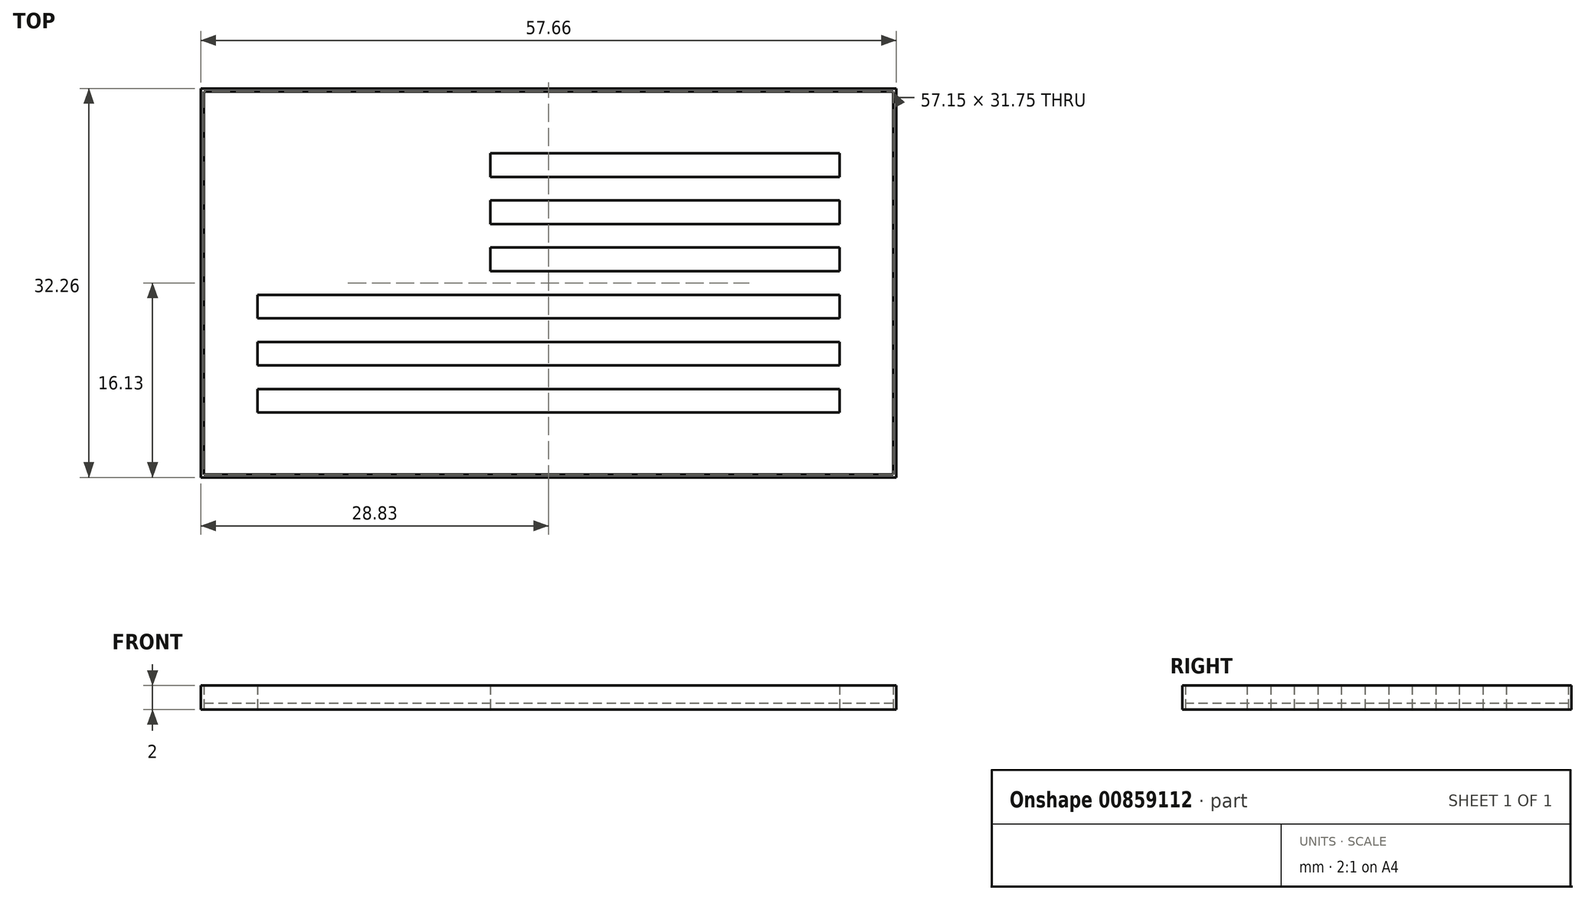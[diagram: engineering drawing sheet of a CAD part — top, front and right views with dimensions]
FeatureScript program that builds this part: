
annotation { "Feature Type Name" : "Feature", "Feature Type Description" : "" }
export const myFeature = defineFeature(function(context is Context, id is Id, definition is map)
    precondition{}
    {
        {
            var Q0;
            Q0=qCreatedBy(makeId("Top.planeOp"),FACE);
            var sketch = newSketch(context, id + "F0", { "sketchPlane" : qUnion([Q0])});
            skLineSegment(sketch, "E0.rect.bottom", {"start": v(24.13, 12.7) * mm, "end": v(-24.13, 12.7) * mm});
            skLineSegment(sketch, "E0.rect.top", {"start": v(24.13, -12.7) * mm, "end": v(-24.13, -12.7) * mm});
            skLineSegment(sketch, "E0.rect.left", {"start": v(24.13, 12.7) * mm, "end": v(24.13, -12.7) * mm});
            skLineSegment(sketch, "E0.rect.right", {"start": v(-24.13, 12.7) * mm, "end": v(-24.13, -12.7) * mm});
            skPoint(sketch, "E0.rect.middle", {"position": v(0, 0) * mm});
            skLineSegment(sketch, "E1.bottom", {"start": v(-24.13, 12.7) * mm, "end": v(-4.83, 12.7) * mm});
            skLineSegment(sketch, "E1.top", {"start": v(-24.13, -0.98) * mm, "end": v(-4.83, -0.98) * mm});
            skLineSegment(sketch, "E1.left", {"start": v(-24.13, 12.7) * mm, "end": v(-24.13, -0.98) * mm});
            skLineSegment(sketch, "E1.right", {"start": v(-4.83, 12.7) * mm, "end": v(-4.83, -0.98) * mm});
            skLineSegment(sketch, "E2.bottom", {"start": v(-4.83, 12.7) * mm, "end": v(24.13, 12.7) * mm});
            skLineSegment(sketch, "E2.top", {"start": v(-4.83, 10.75) * mm, "end": v(24.13, 10.75) * mm});
            skLineSegment(sketch, "E2.left", {"start": v(-4.83, 12.7) * mm, "end": v(-4.83, 10.75) * mm});
            skLineSegment(sketch, "E2.right", {"start": v(24.13, 12.7) * mm, "end": v(24.13, 10.75) * mm});
            skLineSegment(sketch, "E3.MirrorCS", {"start": v(-4.83, 8.8) * mm, "end": v(24.13, 8.8) * mm});
            skLineSegment(sketch, "E4.MirrorCS", {"start": v(-4.83, 6.84) * mm, "end": v(24.13, 6.84) * mm});
            skLineSegment(sketch, "E5.MirrorCS", {"start": v(-4.83, 4.89) * mm, "end": v(24.13, 4.89) * mm});
            skLineSegment(sketch, "E6.MirrorCS", {"start": v(-4.83, 2.93) * mm, "end": v(24.13, 2.93) * mm});
            skLineSegment(sketch, "E7.MirrorCS", {"start": v(-4.83, 0.98) * mm, "end": v(24.13, 0.98) * mm});
            skLineSegment(sketch, "E8.MirrorCS", {"start": v(-4.83, -0.97) * mm, "end": v(24.13, -0.97) * mm});
            skLineSegment(sketch, "E9.bottom", {"start": v(-24.13, -0.98) * mm, "end": v(24.13, -0.98) * mm});
            skLineSegment(sketch, "E9.top", {"start": v(-24.13, -2.93) * mm, "end": v(24.13, -2.93) * mm});
            skLineSegment(sketch, "E9.left", {"start": v(-24.13, -0.98) * mm, "end": v(-24.13, -2.93) * mm});
            skLineSegment(sketch, "E9.right", {"start": v(24.13, -0.98) * mm, "end": v(24.13, -2.93) * mm});
            skLineSegment(sketch, "E10.MirrorCS", {"start": v(-24.13, -4.88) * mm, "end": v(24.13, -4.88) * mm});
            skLineSegment(sketch, "E11.MirrorCS", {"start": v(-24.13, -6.84) * mm, "end": v(24.13, -6.84) * mm});
            skLineSegment(sketch, "E12.MirrorCS", {"start": v(-24.13, -8.8) * mm, "end": v(24.13, -8.8) * mm});
            skLineSegment(sketch, "E13.MirrorCS", {"start": v(-24.13, -10.74) * mm, "end": v(24.13, -10.74) * mm});
            skLineSegment(sketch, "E14.bottom", {"start": v(-24.13, 12.7) * mm, "end": v(-22.53, 12.7) * mm});
            skLineSegment(sketch, "E14.left", {"start": v(-24.13, 12.7) * mm, "end": v(-24.13, 11.33) * mm});
            skPoint(sketch, "E15.cCircle.perimeterSnap0", {"position": v(-22.53, 12.01) * mm});
            skPoint(sketch, "E15.0.startSnap0", {"position": v(-22.53, 12.01) * mm});
            skLineSegment(sketch, "E16", {"start": v(-22.53, 12.12) * mm, "end": v(-22.35, 11.57) * mm});
            skLineSegment(sketch, "E17", {"start": v(-21.78, 11.57) * mm, "end": v(-22.35, 11.57) * mm});
            skLineSegment(sketch, "E18", {"start": v(-23, 10.7) * mm, "end": v(-22.82, 11.24) * mm});
            skLineSegment(sketch, "E19", {"start": v(-23.28, 11.57) * mm, "end": v(-22.82, 11.24) * mm});
            skLineSegment(sketch, "E20", {"start": v(-21.78, 11.57) * mm, "end": v(-22.24, 11.24) * mm});
            skLineSegment(sketch, "E21.trimOffspring", {"start": v(-22.24, 11.24) * mm, "end": v(-22.07, 10.7) * mm});
            skLineSegment(sketch, "E22.trimOffspring", {"start": v(-22.53, 11.03) * mm, "end": v(-23, 10.7) * mm});
            skLineSegment(sketch, "E23.trimOffspring", {"start": v(-22.53, 11.03) * mm, "end": v(-22.07, 10.7) * mm});
            skLineSegment(sketch, "E24.trimOffspring", {"start": v(-22.7, 11.57) * mm, "end": v(-22.53, 12.12) * mm});
            skLineSegment(sketch, "E25.trimOffspring", {"start": v(-22.7, 11.57) * mm, "end": v(-23.28, 11.57) * mm});
            skLineSegment(sketch, "E26.0.1.0", {"start": v(-22.53, 9.37) * mm, "end": v(-22.35, 8.83) * mm});
            skLineSegment(sketch, "E26.0.1.1", {"start": v(-21.78, 8.83) * mm, "end": v(-22.35, 8.83) * mm});
            skLineSegment(sketch, "E26.0.1.2", {"start": v(-21.78, 8.83) * mm, "end": v(-22.24, 8.5) * mm});
            skLineSegment(sketch, "E26.0.1.3", {"start": v(-22.24, 8.5) * mm, "end": v(-22.07, 7.95) * mm});
            skLineSegment(sketch, "E26.0.1.4", {"start": v(-22.53, 8.28) * mm, "end": v(-22.07, 7.95) * mm});
            skLineSegment(sketch, "E26.0.1.5", {"start": v(-22.53, 8.28) * mm, "end": v(-23, 7.95) * mm});
            skLineSegment(sketch, "E26.0.1.6", {"start": v(-23, 7.95) * mm, "end": v(-22.82, 8.5) * mm});
            skLineSegment(sketch, "E26.0.1.7", {"start": v(-23.28, 8.83) * mm, "end": v(-22.82, 8.5) * mm});
            skLineSegment(sketch, "E26.0.1.8", {"start": v(-22.7, 8.83) * mm, "end": v(-22.53, 9.37) * mm});
            skLineSegment(sketch, "E26.0.1.9", {"start": v(-22.7, 8.83) * mm, "end": v(-23.28, 8.83) * mm});
            skLineSegment(sketch, "E26.0.2.0", {"start": v(-22.53, 6.63) * mm, "end": v(-22.35, 6.09) * mm});
            skLineSegment(sketch, "E26.0.2.1", {"start": v(-21.78, 6.09) * mm, "end": v(-22.35, 6.09) * mm});
            skLineSegment(sketch, "E26.0.2.2", {"start": v(-21.78, 6.09) * mm, "end": v(-22.24, 5.75) * mm});
            skLineSegment(sketch, "E26.0.2.3", {"start": v(-22.24, 5.75) * mm, "end": v(-22.07, 5.2) * mm});
            skLineSegment(sketch, "E26.0.2.4", {"start": v(-22.53, 5.54) * mm, "end": v(-22.07, 5.2) * mm});
            skLineSegment(sketch, "E26.0.2.5", {"start": v(-22.53, 5.54) * mm, "end": v(-23, 5.2) * mm});
            skLineSegment(sketch, "E26.0.2.6", {"start": v(-23, 5.2) * mm, "end": v(-22.82, 5.75) * mm});
            skLineSegment(sketch, "E26.0.2.7", {"start": v(-23.28, 6.09) * mm, "end": v(-22.82, 5.75) * mm});
            skLineSegment(sketch, "E26.0.2.8", {"start": v(-22.7, 6.09) * mm, "end": v(-22.53, 6.63) * mm});
            skLineSegment(sketch, "E26.0.2.9", {"start": v(-22.7, 6.09) * mm, "end": v(-23.28, 6.09) * mm});
            skLineSegment(sketch, "E26.0.3.0", {"start": v(-22.53, 3.89) * mm, "end": v(-22.35, 3.34) * mm});
            skLineSegment(sketch, "E26.0.3.1", {"start": v(-21.78, 3.34) * mm, "end": v(-22.35, 3.34) * mm});
            skLineSegment(sketch, "E26.0.3.2", {"start": v(-21.78, 3.34) * mm, "end": v(-22.24, 3) * mm});
            skLineSegment(sketch, "E26.0.3.3", {"start": v(-22.24, 3) * mm, "end": v(-22.07, 2.46) * mm});
            skLineSegment(sketch, "E26.0.3.4", {"start": v(-22.53, 2.8) * mm, "end": v(-22.07, 2.46) * mm});
            skLineSegment(sketch, "E26.0.3.5", {"start": v(-22.53, 2.8) * mm, "end": v(-23, 2.46) * mm});
            skLineSegment(sketch, "E26.0.3.6", {"start": v(-23, 2.46) * mm, "end": v(-22.82, 3) * mm});
            skLineSegment(sketch, "E26.0.3.7", {"start": v(-23.28, 3.34) * mm, "end": v(-22.82, 3) * mm});
            skLineSegment(sketch, "E26.0.3.8", {"start": v(-22.7, 3.34) * mm, "end": v(-22.53, 3.89) * mm});
            skLineSegment(sketch, "E26.0.3.9", {"start": v(-22.7, 3.34) * mm, "end": v(-23.28, 3.34) * mm});
            skLineSegment(sketch, "E26.0.4.0", {"start": v(-22.53, 1.14) * mm, "end": v(-22.35, 0.6) * mm});
            skLineSegment(sketch, "E26.0.4.1", {"start": v(-21.78, 0.6) * mm, "end": v(-22.35, 0.6) * mm});
            skLineSegment(sketch, "E26.0.4.2", {"start": v(-21.78, 0.6) * mm, "end": v(-22.24, 0.26) * mm});
            skLineSegment(sketch, "E26.0.4.3", {"start": v(-22.24, 0.26) * mm, "end": v(-22.07, -0.28) * mm});
            skLineSegment(sketch, "E26.0.4.4", {"start": v(-22.53, 0.05) * mm, "end": v(-22.07, -0.28) * mm});
            skLineSegment(sketch, "E26.0.4.5", {"start": v(-22.53, 0.05) * mm, "end": v(-23, -0.28) * mm});
            skLineSegment(sketch, "E26.0.4.6", {"start": v(-23, -0.28) * mm, "end": v(-22.82, 0.26) * mm});
            skLineSegment(sketch, "E26.0.4.7", {"start": v(-23.28, 0.6) * mm, "end": v(-22.82, 0.26) * mm});
            skLineSegment(sketch, "E26.0.4.8", {"start": v(-22.7, 0.6) * mm, "end": v(-22.53, 1.14) * mm});
            skLineSegment(sketch, "E26.0.4.9", {"start": v(-22.7, 0.6) * mm, "end": v(-23.28, 0.6) * mm});
            skLineSegment(sketch, "E26.1.0.0", {"start": v(-19.33, 12.12) * mm, "end": v(-19.15, 11.57) * mm});
            skLineSegment(sketch, "E26.1.0.1", {"start": v(-18.58, 11.57) * mm, "end": v(-19.15, 11.57) * mm});
            skLineSegment(sketch, "E26.1.0.2", {"start": v(-18.58, 11.57) * mm, "end": v(-19.04, 11.24) * mm});
            skLineSegment(sketch, "E26.1.0.3", {"start": v(-19.04, 11.24) * mm, "end": v(-18.87, 10.7) * mm});
            skLineSegment(sketch, "E26.1.0.4", {"start": v(-19.33, 11.03) * mm, "end": v(-18.87, 10.7) * mm});
            skLineSegment(sketch, "E26.1.0.5", {"start": v(-19.33, 11.03) * mm, "end": v(-19.8, 10.7) * mm});
            skLineSegment(sketch, "E26.1.0.6", {"start": v(-19.8, 10.7) * mm, "end": v(-19.62, 11.24) * mm});
            skLineSegment(sketch, "E26.1.0.7", {"start": v(-20.08, 11.57) * mm, "end": v(-19.62, 11.24) * mm});
            skLineSegment(sketch, "E26.1.0.8", {"start": v(-19.5, 11.57) * mm, "end": v(-19.33, 12.12) * mm});
            skLineSegment(sketch, "E26.1.0.9", {"start": v(-19.5, 11.57) * mm, "end": v(-20.08, 11.57) * mm});
            skLineSegment(sketch, "E26.1.1.0", {"start": v(-19.33, 9.37) * mm, "end": v(-19.15, 8.83) * mm});
            skLineSegment(sketch, "E26.1.1.1", {"start": v(-18.58, 8.83) * mm, "end": v(-19.15, 8.83) * mm});
            skLineSegment(sketch, "E26.1.1.2", {"start": v(-18.58, 8.83) * mm, "end": v(-19.04, 8.5) * mm});
            skLineSegment(sketch, "E26.1.1.3", {"start": v(-19.04, 8.5) * mm, "end": v(-18.87, 7.95) * mm});
            skLineSegment(sketch, "E26.1.1.4", {"start": v(-19.33, 8.28) * mm, "end": v(-18.87, 7.95) * mm});
            skLineSegment(sketch, "E26.1.1.5", {"start": v(-19.33, 8.28) * mm, "end": v(-19.8, 7.95) * mm});
            skLineSegment(sketch, "E26.1.1.6", {"start": v(-19.8, 7.95) * mm, "end": v(-19.62, 8.5) * mm});
            skLineSegment(sketch, "E26.1.1.7", {"start": v(-20.08, 8.83) * mm, "end": v(-19.62, 8.5) * mm});
            skLineSegment(sketch, "E26.1.1.8", {"start": v(-19.5, 8.83) * mm, "end": v(-19.33, 9.37) * mm});
            skLineSegment(sketch, "E26.1.1.9", {"start": v(-19.5, 8.83) * mm, "end": v(-20.08, 8.83) * mm});
            skLineSegment(sketch, "E26.1.2.0", {"start": v(-19.33, 6.63) * mm, "end": v(-19.15, 6.09) * mm});
            skLineSegment(sketch, "E26.1.2.1", {"start": v(-18.58, 6.09) * mm, "end": v(-19.15, 6.09) * mm});
            skLineSegment(sketch, "E26.1.2.2", {"start": v(-18.58, 6.09) * mm, "end": v(-19.04, 5.75) * mm});
            skLineSegment(sketch, "E26.1.2.3", {"start": v(-19.04, 5.75) * mm, "end": v(-18.87, 5.2) * mm});
            skLineSegment(sketch, "E26.1.2.4", {"start": v(-19.33, 5.54) * mm, "end": v(-18.87, 5.2) * mm});
            skLineSegment(sketch, "E26.1.2.5", {"start": v(-19.33, 5.54) * mm, "end": v(-19.8, 5.2) * mm});
            skLineSegment(sketch, "E26.1.2.6", {"start": v(-19.8, 5.2) * mm, "end": v(-19.62, 5.75) * mm});
            skLineSegment(sketch, "E26.1.2.7", {"start": v(-20.08, 6.09) * mm, "end": v(-19.62, 5.75) * mm});
            skLineSegment(sketch, "E26.1.2.8", {"start": v(-19.5, 6.09) * mm, "end": v(-19.33, 6.63) * mm});
            skLineSegment(sketch, "E26.1.2.9", {"start": v(-19.5, 6.09) * mm, "end": v(-20.08, 6.09) * mm});
            skLineSegment(sketch, "E26.1.3.0", {"start": v(-19.33, 3.89) * mm, "end": v(-19.15, 3.34) * mm});
            skLineSegment(sketch, "E26.1.3.1", {"start": v(-18.58, 3.34) * mm, "end": v(-19.15, 3.34) * mm});
            skLineSegment(sketch, "E26.1.3.2", {"start": v(-18.58, 3.34) * mm, "end": v(-19.04, 3) * mm});
            skLineSegment(sketch, "E26.1.3.3", {"start": v(-19.04, 3) * mm, "end": v(-18.87, 2.46) * mm});
            skLineSegment(sketch, "E26.1.3.4", {"start": v(-19.33, 2.8) * mm, "end": v(-18.87, 2.46) * mm});
            skLineSegment(sketch, "E26.1.3.5", {"start": v(-19.33, 2.8) * mm, "end": v(-19.8, 2.46) * mm});
            skLineSegment(sketch, "E26.1.3.6", {"start": v(-19.8, 2.46) * mm, "end": v(-19.62, 3) * mm});
            skLineSegment(sketch, "E26.1.3.7", {"start": v(-20.08, 3.34) * mm, "end": v(-19.62, 3) * mm});
            skLineSegment(sketch, "E26.1.3.8", {"start": v(-19.5, 3.34) * mm, "end": v(-19.33, 3.89) * mm});
            skLineSegment(sketch, "E26.1.3.9", {"start": v(-19.5, 3.34) * mm, "end": v(-20.08, 3.34) * mm});
            skLineSegment(sketch, "E26.1.4.0", {"start": v(-19.33, 1.14) * mm, "end": v(-19.15, 0.6) * mm});
            skLineSegment(sketch, "E26.1.4.1", {"start": v(-18.58, 0.6) * mm, "end": v(-19.15, 0.6) * mm});
            skLineSegment(sketch, "E26.1.4.2", {"start": v(-18.58, 0.6) * mm, "end": v(-19.04, 0.26) * mm});
            skLineSegment(sketch, "E26.1.4.3", {"start": v(-19.04, 0.26) * mm, "end": v(-18.87, -0.28) * mm});
            skLineSegment(sketch, "E26.1.4.4", {"start": v(-19.33, 0.05) * mm, "end": v(-18.87, -0.28) * mm});
            skLineSegment(sketch, "E26.1.4.5", {"start": v(-19.33, 0.05) * mm, "end": v(-19.8, -0.28) * mm});
            skLineSegment(sketch, "E26.1.4.6", {"start": v(-19.8, -0.28) * mm, "end": v(-19.62, 0.26) * mm});
            skLineSegment(sketch, "E26.1.4.7", {"start": v(-20.08, 0.6) * mm, "end": v(-19.62, 0.26) * mm});
            skLineSegment(sketch, "E26.1.4.8", {"start": v(-19.5, 0.6) * mm, "end": v(-19.33, 1.14) * mm});
            skLineSegment(sketch, "E26.1.4.9", {"start": v(-19.5, 0.6) * mm, "end": v(-20.08, 0.6) * mm});
            skLineSegment(sketch, "E26.2.0.0", {"start": v(-16.13, 12.12) * mm, "end": v(-15.95, 11.57) * mm});
            skLineSegment(sketch, "E26.2.0.1", {"start": v(-15.38, 11.57) * mm, "end": v(-15.95, 11.57) * mm});
            skLineSegment(sketch, "E26.2.0.2", {"start": v(-15.38, 11.57) * mm, "end": v(-15.84, 11.24) * mm});
            skLineSegment(sketch, "E26.2.0.3", {"start": v(-15.84, 11.24) * mm, "end": v(-15.67, 10.7) * mm});
            skLineSegment(sketch, "E26.2.0.4", {"start": v(-16.13, 11.03) * mm, "end": v(-15.67, 10.7) * mm});
            skLineSegment(sketch, "E26.2.0.5", {"start": v(-16.13, 11.03) * mm, "end": v(-16.6, 10.7) * mm});
            skLineSegment(sketch, "E26.2.0.6", {"start": v(-16.6, 10.7) * mm, "end": v(-16.42, 11.24) * mm});
            skLineSegment(sketch, "E26.2.0.7", {"start": v(-16.88, 11.57) * mm, "end": v(-16.42, 11.24) * mm});
            skLineSegment(sketch, "E26.2.0.8", {"start": v(-16.3, 11.57) * mm, "end": v(-16.13, 12.12) * mm});
            skLineSegment(sketch, "E26.2.0.9", {"start": v(-16.3, 11.57) * mm, "end": v(-16.88, 11.57) * mm});
            skLineSegment(sketch, "E26.2.1.0", {"start": v(-16.13, 9.37) * mm, "end": v(-15.95, 8.83) * mm});
            skLineSegment(sketch, "E26.2.1.1", {"start": v(-15.38, 8.83) * mm, "end": v(-15.95, 8.83) * mm});
            skLineSegment(sketch, "E26.2.1.2", {"start": v(-15.38, 8.83) * mm, "end": v(-15.84, 8.5) * mm});
            skLineSegment(sketch, "E26.2.1.3", {"start": v(-15.84, 8.5) * mm, "end": v(-15.67, 7.95) * mm});
            skLineSegment(sketch, "E26.2.1.4", {"start": v(-16.13, 8.28) * mm, "end": v(-15.67, 7.95) * mm});
            skLineSegment(sketch, "E26.2.1.5", {"start": v(-16.13, 8.28) * mm, "end": v(-16.6, 7.95) * mm});
            skLineSegment(sketch, "E26.2.1.6", {"start": v(-16.6, 7.95) * mm, "end": v(-16.42, 8.5) * mm});
            skLineSegment(sketch, "E26.2.1.7", {"start": v(-16.88, 8.83) * mm, "end": v(-16.42, 8.5) * mm});
            skLineSegment(sketch, "E26.2.1.8", {"start": v(-16.3, 8.83) * mm, "end": v(-16.13, 9.37) * mm});
            skLineSegment(sketch, "E26.2.1.9", {"start": v(-16.3, 8.83) * mm, "end": v(-16.88, 8.83) * mm});
            skLineSegment(sketch, "E26.2.2.0", {"start": v(-16.13, 6.63) * mm, "end": v(-15.95, 6.09) * mm});
            skLineSegment(sketch, "E26.2.2.1", {"start": v(-15.38, 6.09) * mm, "end": v(-15.95, 6.09) * mm});
            skLineSegment(sketch, "E26.2.2.2", {"start": v(-15.38, 6.09) * mm, "end": v(-15.84, 5.75) * mm});
            skLineSegment(sketch, "E26.2.2.3", {"start": v(-15.84, 5.75) * mm, "end": v(-15.67, 5.2) * mm});
            skLineSegment(sketch, "E26.2.2.4", {"start": v(-16.13, 5.54) * mm, "end": v(-15.67, 5.2) * mm});
            skLineSegment(sketch, "E26.2.2.5", {"start": v(-16.13, 5.54) * mm, "end": v(-16.6, 5.2) * mm});
            skLineSegment(sketch, "E26.2.2.6", {"start": v(-16.6, 5.2) * mm, "end": v(-16.42, 5.75) * mm});
            skLineSegment(sketch, "E26.2.2.7", {"start": v(-16.88, 6.09) * mm, "end": v(-16.42, 5.75) * mm});
            skLineSegment(sketch, "E26.2.2.8", {"start": v(-16.3, 6.09) * mm, "end": v(-16.13, 6.63) * mm});
            skLineSegment(sketch, "E26.2.2.9", {"start": v(-16.3, 6.09) * mm, "end": v(-16.88, 6.09) * mm});
            skLineSegment(sketch, "E26.2.3.0", {"start": v(-16.13, 3.89) * mm, "end": v(-15.95, 3.34) * mm});
            skLineSegment(sketch, "E26.2.3.1", {"start": v(-15.38, 3.34) * mm, "end": v(-15.95, 3.34) * mm});
            skLineSegment(sketch, "E26.2.3.2", {"start": v(-15.38, 3.34) * mm, "end": v(-15.84, 3) * mm});
            skLineSegment(sketch, "E26.2.3.3", {"start": v(-15.84, 3) * mm, "end": v(-15.67, 2.46) * mm});
            skLineSegment(sketch, "E26.2.3.4", {"start": v(-16.13, 2.8) * mm, "end": v(-15.67, 2.46) * mm});
            skLineSegment(sketch, "E26.2.3.5", {"start": v(-16.13, 2.8) * mm, "end": v(-16.6, 2.46) * mm});
            skLineSegment(sketch, "E26.2.3.6", {"start": v(-16.6, 2.46) * mm, "end": v(-16.42, 3) * mm});
            skLineSegment(sketch, "E26.2.3.7", {"start": v(-16.88, 3.34) * mm, "end": v(-16.42, 3) * mm});
            skLineSegment(sketch, "E26.2.3.8", {"start": v(-16.3, 3.34) * mm, "end": v(-16.13, 3.89) * mm});
            skLineSegment(sketch, "E26.2.3.9", {"start": v(-16.3, 3.34) * mm, "end": v(-16.88, 3.34) * mm});
            skLineSegment(sketch, "E26.2.4.0", {"start": v(-16.13, 1.14) * mm, "end": v(-15.95, 0.6) * mm});
            skLineSegment(sketch, "E26.2.4.1", {"start": v(-15.38, 0.6) * mm, "end": v(-15.95, 0.6) * mm});
            skLineSegment(sketch, "E26.2.4.2", {"start": v(-15.38, 0.6) * mm, "end": v(-15.84, 0.26) * mm});
            skLineSegment(sketch, "E26.2.4.3", {"start": v(-15.84, 0.26) * mm, "end": v(-15.67, -0.28) * mm});
            skLineSegment(sketch, "E26.2.4.4", {"start": v(-16.13, 0.05) * mm, "end": v(-15.67, -0.28) * mm});
            skLineSegment(sketch, "E26.2.4.5", {"start": v(-16.13, 0.05) * mm, "end": v(-16.6, -0.28) * mm});
            skLineSegment(sketch, "E26.2.4.6", {"start": v(-16.6, -0.28) * mm, "end": v(-16.42, 0.26) * mm});
            skLineSegment(sketch, "E26.2.4.7", {"start": v(-16.88, 0.6) * mm, "end": v(-16.42, 0.26) * mm});
            skLineSegment(sketch, "E26.2.4.8", {"start": v(-16.3, 0.6) * mm, "end": v(-16.13, 1.14) * mm});
            skLineSegment(sketch, "E26.2.4.9", {"start": v(-16.3, 0.6) * mm, "end": v(-16.88, 0.6) * mm});
            skLineSegment(sketch, "E26.3.0.0", {"start": v(-12.93, 12.12) * mm, "end": v(-12.75, 11.57) * mm});
            skLineSegment(sketch, "E26.3.0.1", {"start": v(-12.18, 11.57) * mm, "end": v(-12.75, 11.57) * mm});
            skLineSegment(sketch, "E26.3.0.2", {"start": v(-12.18, 11.57) * mm, "end": v(-12.64, 11.24) * mm});
            skLineSegment(sketch, "E26.3.0.3", {"start": v(-12.64, 11.24) * mm, "end": v(-12.47, 10.7) * mm});
            skLineSegment(sketch, "E26.3.0.4", {"start": v(-12.93, 11.03) * mm, "end": v(-12.47, 10.7) * mm});
            skLineSegment(sketch, "E26.3.0.5", {"start": v(-12.93, 11.03) * mm, "end": v(-13.4, 10.7) * mm});
            skLineSegment(sketch, "E26.3.0.6", {"start": v(-13.4, 10.7) * mm, "end": v(-13.21, 11.24) * mm});
            skLineSegment(sketch, "E26.3.0.7", {"start": v(-13.68, 11.57) * mm, "end": v(-13.21, 11.24) * mm});
            skLineSegment(sketch, "E26.3.0.8", {"start": v(-13.1, 11.57) * mm, "end": v(-12.93, 12.12) * mm});
            skLineSegment(sketch, "E26.3.0.9", {"start": v(-13.1, 11.57) * mm, "end": v(-13.68, 11.57) * mm});
            skLineSegment(sketch, "E26.3.1.0", {"start": v(-12.93, 9.37) * mm, "end": v(-12.75, 8.83) * mm});
            skLineSegment(sketch, "E26.3.1.1", {"start": v(-12.18, 8.83) * mm, "end": v(-12.75, 8.83) * mm});
            skLineSegment(sketch, "E26.3.1.2", {"start": v(-12.18, 8.83) * mm, "end": v(-12.64, 8.5) * mm});
            skLineSegment(sketch, "E26.3.1.3", {"start": v(-12.64, 8.5) * mm, "end": v(-12.47, 7.95) * mm});
            skLineSegment(sketch, "E26.3.1.4", {"start": v(-12.93, 8.28) * mm, "end": v(-12.47, 7.95) * mm});
            skLineSegment(sketch, "E26.3.1.5", {"start": v(-12.93, 8.28) * mm, "end": v(-13.4, 7.95) * mm});
            skLineSegment(sketch, "E26.3.1.6", {"start": v(-13.4, 7.95) * mm, "end": v(-13.21, 8.5) * mm});
            skLineSegment(sketch, "E26.3.1.7", {"start": v(-13.68, 8.83) * mm, "end": v(-13.21, 8.5) * mm});
            skLineSegment(sketch, "E26.3.1.8", {"start": v(-13.1, 8.83) * mm, "end": v(-12.93, 9.37) * mm});
            skLineSegment(sketch, "E26.3.1.9", {"start": v(-13.1, 8.83) * mm, "end": v(-13.68, 8.83) * mm});
            skLineSegment(sketch, "E26.3.2.0", {"start": v(-12.93, 6.63) * mm, "end": v(-12.75, 6.09) * mm});
            skLineSegment(sketch, "E26.3.2.1", {"start": v(-12.18, 6.09) * mm, "end": v(-12.75, 6.09) * mm});
            skLineSegment(sketch, "E26.3.2.2", {"start": v(-12.18, 6.09) * mm, "end": v(-12.64, 5.75) * mm});
            skLineSegment(sketch, "E26.3.2.3", {"start": v(-12.64, 5.75) * mm, "end": v(-12.47, 5.2) * mm});
            skLineSegment(sketch, "E26.3.2.4", {"start": v(-12.93, 5.54) * mm, "end": v(-12.47, 5.2) * mm});
            skLineSegment(sketch, "E26.3.2.5", {"start": v(-12.93, 5.54) * mm, "end": v(-13.4, 5.2) * mm});
            skLineSegment(sketch, "E26.3.2.6", {"start": v(-13.4, 5.2) * mm, "end": v(-13.21, 5.75) * mm});
            skLineSegment(sketch, "E26.3.2.7", {"start": v(-13.68, 6.09) * mm, "end": v(-13.21, 5.75) * mm});
            skLineSegment(sketch, "E26.3.2.8", {"start": v(-13.1, 6.09) * mm, "end": v(-12.93, 6.63) * mm});
            skLineSegment(sketch, "E26.3.2.9", {"start": v(-13.1, 6.09) * mm, "end": v(-13.68, 6.09) * mm});
            skLineSegment(sketch, "E26.3.3.0", {"start": v(-12.93, 3.89) * mm, "end": v(-12.75, 3.34) * mm});
            skLineSegment(sketch, "E26.3.3.1", {"start": v(-12.18, 3.34) * mm, "end": v(-12.75, 3.34) * mm});
            skLineSegment(sketch, "E26.3.3.2", {"start": v(-12.18, 3.34) * mm, "end": v(-12.64, 3) * mm});
            skLineSegment(sketch, "E26.3.3.3", {"start": v(-12.64, 3) * mm, "end": v(-12.47, 2.46) * mm});
            skLineSegment(sketch, "E26.3.3.4", {"start": v(-12.93, 2.8) * mm, "end": v(-12.47, 2.46) * mm});
            skLineSegment(sketch, "E26.3.3.5", {"start": v(-12.93, 2.8) * mm, "end": v(-13.4, 2.46) * mm});
            skLineSegment(sketch, "E26.3.3.6", {"start": v(-13.4, 2.46) * mm, "end": v(-13.21, 3) * mm});
            skLineSegment(sketch, "E26.3.3.7", {"start": v(-13.68, 3.34) * mm, "end": v(-13.21, 3) * mm});
            skLineSegment(sketch, "E26.3.3.8", {"start": v(-13.1, 3.34) * mm, "end": v(-12.93, 3.89) * mm});
            skLineSegment(sketch, "E26.3.3.9", {"start": v(-13.1, 3.34) * mm, "end": v(-13.68, 3.34) * mm});
            skLineSegment(sketch, "E26.3.4.0", {"start": v(-12.93, 1.14) * mm, "end": v(-12.75, 0.6) * mm});
            skLineSegment(sketch, "E26.3.4.1", {"start": v(-12.18, 0.6) * mm, "end": v(-12.75, 0.6) * mm});
            skLineSegment(sketch, "E26.3.4.2", {"start": v(-12.18, 0.6) * mm, "end": v(-12.64, 0.26) * mm});
            skLineSegment(sketch, "E26.3.4.3", {"start": v(-12.64, 0.26) * mm, "end": v(-12.47, -0.28) * mm});
            skLineSegment(sketch, "E26.3.4.4", {"start": v(-12.93, 0.05) * mm, "end": v(-12.47, -0.28) * mm});
            skLineSegment(sketch, "E26.3.4.5", {"start": v(-12.93, 0.05) * mm, "end": v(-13.4, -0.28) * mm});
            skLineSegment(sketch, "E26.3.4.6", {"start": v(-13.4, -0.28) * mm, "end": v(-13.21, 0.26) * mm});
            skLineSegment(sketch, "E26.3.4.7", {"start": v(-13.68, 0.6) * mm, "end": v(-13.21, 0.26) * mm});
            skLineSegment(sketch, "E26.3.4.8", {"start": v(-13.1, 0.6) * mm, "end": v(-12.93, 1.14) * mm});
            skLineSegment(sketch, "E26.3.4.9", {"start": v(-13.1, 0.6) * mm, "end": v(-13.68, 0.6) * mm});
            skLineSegment(sketch, "E26.4.0.0", {"start": v(-9.73, 12.12) * mm, "end": v(-9.55, 11.57) * mm});
            skLineSegment(sketch, "E26.4.0.1", {"start": v(-8.98, 11.57) * mm, "end": v(-9.55, 11.57) * mm});
            skLineSegment(sketch, "E26.4.0.2", {"start": v(-8.98, 11.57) * mm, "end": v(-9.44, 11.24) * mm});
            skLineSegment(sketch, "E26.4.0.3", {"start": v(-9.44, 11.24) * mm, "end": v(-9.27, 10.7) * mm});
            skLineSegment(sketch, "E26.4.0.4", {"start": v(-9.73, 11.03) * mm, "end": v(-9.27, 10.7) * mm});
            skLineSegment(sketch, "E26.4.0.5", {"start": v(-9.73, 11.03) * mm, "end": v(-10.2, 10.7) * mm});
            skLineSegment(sketch, "E26.4.0.6", {"start": v(-10.2, 10.7) * mm, "end": v(-10.01, 11.24) * mm});
            skLineSegment(sketch, "E26.4.0.7", {"start": v(-10.48, 11.57) * mm, "end": v(-10.01, 11.24) * mm});
            skLineSegment(sketch, "E26.4.0.8", {"start": v(-9.9, 11.57) * mm, "end": v(-9.73, 12.12) * mm});
            skLineSegment(sketch, "E26.4.0.9", {"start": v(-9.9, 11.57) * mm, "end": v(-10.48, 11.57) * mm});
            skLineSegment(sketch, "E26.4.1.0", {"start": v(-9.73, 9.37) * mm, "end": v(-9.55, 8.83) * mm});
            skLineSegment(sketch, "E26.4.1.1", {"start": v(-8.98, 8.83) * mm, "end": v(-9.55, 8.83) * mm});
            skLineSegment(sketch, "E26.4.1.2", {"start": v(-8.98, 8.83) * mm, "end": v(-9.44, 8.5) * mm});
            skLineSegment(sketch, "E26.4.1.3", {"start": v(-9.44, 8.5) * mm, "end": v(-9.27, 7.95) * mm});
            skLineSegment(sketch, "E26.4.1.4", {"start": v(-9.73, 8.28) * mm, "end": v(-9.27, 7.95) * mm});
            skLineSegment(sketch, "E26.4.1.5", {"start": v(-9.73, 8.28) * mm, "end": v(-10.2, 7.95) * mm});
            skLineSegment(sketch, "E26.4.1.6", {"start": v(-10.2, 7.95) * mm, "end": v(-10.01, 8.5) * mm});
            skLineSegment(sketch, "E26.4.1.7", {"start": v(-10.48, 8.83) * mm, "end": v(-10.01, 8.5) * mm});
            skLineSegment(sketch, "E26.4.1.8", {"start": v(-9.9, 8.83) * mm, "end": v(-9.73, 9.37) * mm});
            skLineSegment(sketch, "E26.4.1.9", {"start": v(-9.9, 8.83) * mm, "end": v(-10.48, 8.83) * mm});
            skLineSegment(sketch, "E26.4.2.0", {"start": v(-9.73, 6.63) * mm, "end": v(-9.55, 6.09) * mm});
            skLineSegment(sketch, "E26.4.2.1", {"start": v(-8.98, 6.09) * mm, "end": v(-9.55, 6.09) * mm});
            skLineSegment(sketch, "E26.4.2.2", {"start": v(-8.98, 6.09) * mm, "end": v(-9.44, 5.75) * mm});
            skLineSegment(sketch, "E26.4.2.3", {"start": v(-9.44, 5.75) * mm, "end": v(-9.27, 5.2) * mm});
            skLineSegment(sketch, "E26.4.2.4", {"start": v(-9.73, 5.54) * mm, "end": v(-9.27, 5.2) * mm});
            skLineSegment(sketch, "E26.4.2.5", {"start": v(-9.73, 5.54) * mm, "end": v(-10.2, 5.2) * mm});
            skLineSegment(sketch, "E26.4.2.6", {"start": v(-10.2, 5.2) * mm, "end": v(-10.01, 5.75) * mm});
            skLineSegment(sketch, "E26.4.2.7", {"start": v(-10.48, 6.09) * mm, "end": v(-10.01, 5.75) * mm});
            skLineSegment(sketch, "E26.4.2.8", {"start": v(-9.9, 6.09) * mm, "end": v(-9.73, 6.63) * mm});
            skLineSegment(sketch, "E26.4.2.9", {"start": v(-9.9, 6.09) * mm, "end": v(-10.48, 6.09) * mm});
            skLineSegment(sketch, "E26.4.3.0", {"start": v(-9.73, 3.89) * mm, "end": v(-9.55, 3.34) * mm});
            skLineSegment(sketch, "E26.4.3.1", {"start": v(-8.98, 3.34) * mm, "end": v(-9.55, 3.34) * mm});
            skLineSegment(sketch, "E26.4.3.2", {"start": v(-8.98, 3.34) * mm, "end": v(-9.44, 3) * mm});
            skLineSegment(sketch, "E26.4.3.3", {"start": v(-9.44, 3) * mm, "end": v(-9.27, 2.46) * mm});
            skLineSegment(sketch, "E26.4.3.4", {"start": v(-9.73, 2.8) * mm, "end": v(-9.27, 2.46) * mm});
            skLineSegment(sketch, "E26.4.3.5", {"start": v(-9.73, 2.8) * mm, "end": v(-10.2, 2.46) * mm});
            skLineSegment(sketch, "E26.4.3.6", {"start": v(-10.2, 2.46) * mm, "end": v(-10.01, 3) * mm});
            skLineSegment(sketch, "E26.4.3.7", {"start": v(-10.48, 3.34) * mm, "end": v(-10.01, 3) * mm});
            skLineSegment(sketch, "E26.4.3.8", {"start": v(-9.9, 3.34) * mm, "end": v(-9.73, 3.89) * mm});
            skLineSegment(sketch, "E26.4.3.9", {"start": v(-9.9, 3.34) * mm, "end": v(-10.48, 3.34) * mm});
            skLineSegment(sketch, "E26.4.4.0", {"start": v(-9.73, 1.14) * mm, "end": v(-9.55, 0.6) * mm});
            skLineSegment(sketch, "E26.4.4.1", {"start": v(-8.98, 0.6) * mm, "end": v(-9.55, 0.6) * mm});
            skLineSegment(sketch, "E26.4.4.2", {"start": v(-8.98, 0.6) * mm, "end": v(-9.44, 0.26) * mm});
            skLineSegment(sketch, "E26.4.4.3", {"start": v(-9.44, 0.26) * mm, "end": v(-9.27, -0.28) * mm});
            skLineSegment(sketch, "E26.4.4.4", {"start": v(-9.73, 0.05) * mm, "end": v(-9.27, -0.28) * mm});
            skLineSegment(sketch, "E26.4.4.5", {"start": v(-9.73, 0.05) * mm, "end": v(-10.2, -0.28) * mm});
            skLineSegment(sketch, "E26.4.4.6", {"start": v(-10.2, -0.28) * mm, "end": v(-10.01, 0.26) * mm});
            skLineSegment(sketch, "E26.4.4.7", {"start": v(-10.48, 0.6) * mm, "end": v(-10.01, 0.26) * mm});
            skLineSegment(sketch, "E26.4.4.8", {"start": v(-9.9, 0.6) * mm, "end": v(-9.73, 1.14) * mm});
            skLineSegment(sketch, "E26.4.4.9", {"start": v(-9.9, 0.6) * mm, "end": v(-10.48, 0.6) * mm});
            skLineSegment(sketch, "E26.5.0.0", {"start": v(-6.53, 12.12) * mm, "end": v(-6.35, 11.57) * mm});
            skLineSegment(sketch, "E26.5.0.1", {"start": v(-5.78, 11.57) * mm, "end": v(-6.35, 11.57) * mm});
            skLineSegment(sketch, "E26.5.0.2", {"start": v(-5.78, 11.57) * mm, "end": v(-6.24, 11.24) * mm});
            skLineSegment(sketch, "E26.5.0.3", {"start": v(-6.24, 11.24) * mm, "end": v(-6.06, 10.7) * mm});
            skLineSegment(sketch, "E26.5.0.4", {"start": v(-6.53, 11.03) * mm, "end": v(-6.06, 10.7) * mm});
            skLineSegment(sketch, "E26.5.0.5", {"start": v(-6.53, 11.03) * mm, "end": v(-7, 10.7) * mm});
            skLineSegment(sketch, "E26.5.0.6", {"start": v(-7, 10.7) * mm, "end": v(-6.81, 11.24) * mm});
            skLineSegment(sketch, "E26.5.0.7", {"start": v(-7.28, 11.57) * mm, "end": v(-6.81, 11.24) * mm});
            skLineSegment(sketch, "E26.5.0.8", {"start": v(-6.7, 11.57) * mm, "end": v(-6.53, 12.12) * mm});
            skLineSegment(sketch, "E26.5.0.9", {"start": v(-6.7, 11.57) * mm, "end": v(-7.28, 11.57) * mm});
            skLineSegment(sketch, "E26.5.1.0", {"start": v(-6.53, 9.37) * mm, "end": v(-6.35, 8.83) * mm});
            skLineSegment(sketch, "E26.5.1.1", {"start": v(-5.78, 8.83) * mm, "end": v(-6.35, 8.83) * mm});
            skLineSegment(sketch, "E26.5.1.2", {"start": v(-5.78, 8.83) * mm, "end": v(-6.24, 8.5) * mm});
            skLineSegment(sketch, "E26.5.1.3", {"start": v(-6.24, 8.5) * mm, "end": v(-6.06, 7.95) * mm});
            skLineSegment(sketch, "E26.5.1.4", {"start": v(-6.53, 8.28) * mm, "end": v(-6.06, 7.95) * mm});
            skLineSegment(sketch, "E26.5.1.5", {"start": v(-6.53, 8.28) * mm, "end": v(-7, 7.95) * mm});
            skLineSegment(sketch, "E26.5.1.6", {"start": v(-7, 7.95) * mm, "end": v(-6.81, 8.5) * mm});
            skLineSegment(sketch, "E26.5.1.7", {"start": v(-7.28, 8.83) * mm, "end": v(-6.81, 8.5) * mm});
            skLineSegment(sketch, "E26.5.1.8", {"start": v(-6.7, 8.83) * mm, "end": v(-6.53, 9.37) * mm});
            skLineSegment(sketch, "E26.5.1.9", {"start": v(-6.7, 8.83) * mm, "end": v(-7.28, 8.83) * mm});
            skLineSegment(sketch, "E26.5.2.0", {"start": v(-6.53, 6.63) * mm, "end": v(-6.35, 6.09) * mm});
            skLineSegment(sketch, "E26.5.2.1", {"start": v(-5.78, 6.09) * mm, "end": v(-6.35, 6.09) * mm});
            skLineSegment(sketch, "E26.5.2.2", {"start": v(-5.78, 6.09) * mm, "end": v(-6.24, 5.75) * mm});
            skLineSegment(sketch, "E26.5.2.3", {"start": v(-6.24, 5.75) * mm, "end": v(-6.06, 5.2) * mm});
            skLineSegment(sketch, "E26.5.2.4", {"start": v(-6.53, 5.54) * mm, "end": v(-6.06, 5.2) * mm});
            skLineSegment(sketch, "E26.5.2.5", {"start": v(-6.53, 5.54) * mm, "end": v(-7, 5.2) * mm});
            skLineSegment(sketch, "E26.5.2.6", {"start": v(-7, 5.2) * mm, "end": v(-6.81, 5.75) * mm});
            skLineSegment(sketch, "E26.5.2.7", {"start": v(-7.28, 6.09) * mm, "end": v(-6.81, 5.75) * mm});
            skLineSegment(sketch, "E26.5.2.8", {"start": v(-6.7, 6.09) * mm, "end": v(-6.53, 6.63) * mm});
            skLineSegment(sketch, "E26.5.2.9", {"start": v(-6.7, 6.09) * mm, "end": v(-7.28, 6.09) * mm});
            skLineSegment(sketch, "E26.5.3.0", {"start": v(-6.53, 3.89) * mm, "end": v(-6.35, 3.34) * mm});
            skLineSegment(sketch, "E26.5.3.1", {"start": v(-5.78, 3.34) * mm, "end": v(-6.35, 3.34) * mm});
            skLineSegment(sketch, "E26.5.3.2", {"start": v(-5.78, 3.34) * mm, "end": v(-6.24, 3) * mm});
            skLineSegment(sketch, "E26.5.3.3", {"start": v(-6.24, 3) * mm, "end": v(-6.06, 2.46) * mm});
            skLineSegment(sketch, "E26.5.3.4", {"start": v(-6.53, 2.8) * mm, "end": v(-6.06, 2.46) * mm});
            skLineSegment(sketch, "E26.5.3.5", {"start": v(-6.53, 2.8) * mm, "end": v(-7, 2.46) * mm});
            skLineSegment(sketch, "E26.5.3.6", {"start": v(-7, 2.46) * mm, "end": v(-6.81, 3) * mm});
            skLineSegment(sketch, "E26.5.3.7", {"start": v(-7.28, 3.34) * mm, "end": v(-6.81, 3) * mm});
            skLineSegment(sketch, "E26.5.3.8", {"start": v(-6.7, 3.34) * mm, "end": v(-6.53, 3.89) * mm});
            skLineSegment(sketch, "E26.5.3.9", {"start": v(-6.7, 3.34) * mm, "end": v(-7.28, 3.34) * mm});
            skLineSegment(sketch, "E26.5.4.0", {"start": v(-6.53, 1.14) * mm, "end": v(-6.35, 0.6) * mm});
            skLineSegment(sketch, "E26.5.4.1", {"start": v(-5.78, 0.6) * mm, "end": v(-6.35, 0.6) * mm});
            skLineSegment(sketch, "E26.5.4.2", {"start": v(-5.78, 0.6) * mm, "end": v(-6.24, 0.26) * mm});
            skLineSegment(sketch, "E26.5.4.3", {"start": v(-6.24, 0.26) * mm, "end": v(-6.06, -0.28) * mm});
            skLineSegment(sketch, "E26.5.4.4", {"start": v(-6.53, 0.05) * mm, "end": v(-6.06, -0.28) * mm});
            skLineSegment(sketch, "E26.5.4.5", {"start": v(-6.53, 0.05) * mm, "end": v(-7, -0.28) * mm});
            skLineSegment(sketch, "E26.5.4.6", {"start": v(-7, -0.28) * mm, "end": v(-6.81, 0.26) * mm});
            skLineSegment(sketch, "E26.5.4.7", {"start": v(-7.28, 0.6) * mm, "end": v(-6.81, 0.26) * mm});
            skLineSegment(sketch, "E26.5.4.8", {"start": v(-6.7, 0.6) * mm, "end": v(-6.53, 1.14) * mm});
            skLineSegment(sketch, "E26.5.4.9", {"start": v(-6.7, 0.6) * mm, "end": v(-7.28, 0.6) * mm});
            skLineSegment(sketch, "E26.direction1", {"start": v(-22.35, 11.57) * mm, "end": v(-19.15, 11.57) * mm, "construction": true});
            skLineSegment(sketch, "E26.direction2", {"start": v(-22.35, 11.57) * mm, "end": v(-22.35, 8.83) * mm, "construction": true});
            skPoint(sketch, "E27.cCircle.perimeterSnap0", {"position": v(-20.93, 10.64) * mm});
            skPoint(sketch, "E27.0.startSnap0", {"position": v(-20.93, 10.64) * mm});
            skLineSegment(sketch, "E28", {"start": v(-20.93, 10.75) * mm, "end": v(-20.75, 10.2) * mm});
            skLineSegment(sketch, "E29", {"start": v(-21.68, 10.2) * mm, "end": v(-21.1, 10.2) * mm});
            skLineSegment(sketch, "E30", {"start": v(-21.4, 9.32) * mm, "end": v(-20.93, 9.66) * mm});
            skLineSegment(sketch, "E31", {"start": v(-21.4, 9.32) * mm, "end": v(-21.22, 9.86) * mm});
            skLineSegment(sketch, "E32", {"start": v(-20.47, 9.32) * mm, "end": v(-20.93, 9.66) * mm});
            skLineSegment(sketch, "E33.trimOffspring", {"start": v(-20.64, 9.86) * mm, "end": v(-20.47, 9.32) * mm});
            skLineSegment(sketch, "E34.trimOffspring", {"start": v(-20.75, 10.2) * mm, "end": v(-20.18, 10.2) * mm});
            skLineSegment(sketch, "E35.trimOffspring", {"start": v(-21.1, 10.2) * mm, "end": v(-20.93, 10.75) * mm});
            skLineSegment(sketch, "E36.trimOffspring", {"start": v(-21.22, 9.86) * mm, "end": v(-21.68, 10.2) * mm});
            skLineSegment(sketch, "E37.trimOffspring", {"start": v(-20.64, 9.86) * mm, "end": v(-20.18, 10.2) * mm});
            skLineSegment(sketch, "E38.0.1.0", {"start": v(-20.93, 8) * mm, "end": v(-20.75, 7.46) * mm});
            skLineSegment(sketch, "E38.0.1.1", {"start": v(-20.75, 7.46) * mm, "end": v(-20.18, 7.46) * mm});
            skLineSegment(sketch, "E38.0.1.2", {"start": v(-20.64, 7.12) * mm, "end": v(-20.18, 7.46) * mm});
            skLineSegment(sketch, "E38.0.1.3", {"start": v(-20.64, 7.12) * mm, "end": v(-20.47, 6.57) * mm});
            skLineSegment(sketch, "E38.0.1.4", {"start": v(-20.47, 6.57) * mm, "end": v(-20.93, 6.91) * mm});
            skLineSegment(sketch, "E38.0.1.5", {"start": v(-21.4, 6.57) * mm, "end": v(-20.93, 6.91) * mm});
            skLineSegment(sketch, "E38.0.1.6", {"start": v(-21.4, 6.57) * mm, "end": v(-21.22, 7.12) * mm});
            skLineSegment(sketch, "E38.0.1.7", {"start": v(-21.22, 7.12) * mm, "end": v(-21.68, 7.46) * mm});
            skLineSegment(sketch, "E38.0.1.8", {"start": v(-21.68, 7.46) * mm, "end": v(-21.1, 7.46) * mm});
            skLineSegment(sketch, "E38.0.1.9", {"start": v(-21.1, 7.46) * mm, "end": v(-20.93, 8) * mm});
            skLineSegment(sketch, "E38.0.2.0", {"start": v(-20.93, 5.26) * mm, "end": v(-20.75, 4.71) * mm});
            skLineSegment(sketch, "E38.0.2.1", {"start": v(-20.75, 4.71) * mm, "end": v(-20.18, 4.71) * mm});
            skLineSegment(sketch, "E38.0.2.2", {"start": v(-20.64, 4.38) * mm, "end": v(-20.18, 4.71) * mm});
            skLineSegment(sketch, "E38.0.2.3", {"start": v(-20.64, 4.38) * mm, "end": v(-20.47, 3.83) * mm});
            skLineSegment(sketch, "E38.0.2.4", {"start": v(-20.47, 3.83) * mm, "end": v(-20.93, 4.17) * mm});
            skLineSegment(sketch, "E38.0.2.5", {"start": v(-21.4, 3.83) * mm, "end": v(-20.93, 4.17) * mm});
            skLineSegment(sketch, "E38.0.2.6", {"start": v(-21.4, 3.83) * mm, "end": v(-21.22, 4.38) * mm});
            skLineSegment(sketch, "E38.0.2.7", {"start": v(-21.22, 4.38) * mm, "end": v(-21.68, 4.71) * mm});
            skLineSegment(sketch, "E38.0.2.8", {"start": v(-21.68, 4.71) * mm, "end": v(-21.1, 4.71) * mm});
            skLineSegment(sketch, "E38.0.2.9", {"start": v(-21.1, 4.71) * mm, "end": v(-20.93, 5.26) * mm});
            skLineSegment(sketch, "E38.0.3.0", {"start": v(-20.93, 2.52) * mm, "end": v(-20.75, 1.97) * mm});
            skLineSegment(sketch, "E38.0.3.1", {"start": v(-20.75, 1.97) * mm, "end": v(-20.18, 1.97) * mm});
            skLineSegment(sketch, "E38.0.3.2", {"start": v(-20.64, 1.63) * mm, "end": v(-20.18, 1.97) * mm});
            skLineSegment(sketch, "E38.0.3.3", {"start": v(-20.64, 1.63) * mm, "end": v(-20.47, 1.09) * mm});
            skLineSegment(sketch, "E38.0.3.4", {"start": v(-20.47, 1.09) * mm, "end": v(-20.93, 1.43) * mm});
            skLineSegment(sketch, "E38.0.3.5", {"start": v(-21.4, 1.09) * mm, "end": v(-20.93, 1.43) * mm});
            skLineSegment(sketch, "E38.0.3.6", {"start": v(-21.4, 1.09) * mm, "end": v(-21.22, 1.63) * mm});
            skLineSegment(sketch, "E38.0.3.7", {"start": v(-21.22, 1.63) * mm, "end": v(-21.68, 1.97) * mm});
            skLineSegment(sketch, "E38.0.3.8", {"start": v(-21.68, 1.97) * mm, "end": v(-21.1, 1.97) * mm});
            skLineSegment(sketch, "E38.0.3.9", {"start": v(-21.1, 1.97) * mm, "end": v(-20.93, 2.52) * mm});
            skLineSegment(sketch, "E38.1.0.0", {"start": v(-17.73, 10.75) * mm, "end": v(-17.55, 10.2) * mm});
            skLineSegment(sketch, "E38.1.0.1", {"start": v(-17.55, 10.2) * mm, "end": v(-16.98, 10.2) * mm});
            skLineSegment(sketch, "E38.1.0.2", {"start": v(-17.44, 9.86) * mm, "end": v(-16.98, 10.2) * mm});
            skLineSegment(sketch, "E38.1.0.3", {"start": v(-17.44, 9.86) * mm, "end": v(-17.26, 9.32) * mm});
            skLineSegment(sketch, "E38.1.0.4", {"start": v(-17.26, 9.32) * mm, "end": v(-17.73, 9.66) * mm});
            skLineSegment(sketch, "E38.1.0.5", {"start": v(-18.2, 9.32) * mm, "end": v(-17.73, 9.66) * mm});
            skLineSegment(sketch, "E38.1.0.6", {"start": v(-18.2, 9.32) * mm, "end": v(-18.02, 9.86) * mm});
            skLineSegment(sketch, "E38.1.0.7", {"start": v(-18.02, 9.86) * mm, "end": v(-18.48, 10.2) * mm});
            skLineSegment(sketch, "E38.1.0.8", {"start": v(-18.48, 10.2) * mm, "end": v(-17.9, 10.2) * mm});
            skLineSegment(sketch, "E38.1.0.9", {"start": v(-17.9, 10.2) * mm, "end": v(-17.73, 10.75) * mm});
            skLineSegment(sketch, "E38.1.1.0", {"start": v(-17.73, 8) * mm, "end": v(-17.55, 7.46) * mm});
            skLineSegment(sketch, "E38.1.1.1", {"start": v(-17.55, 7.46) * mm, "end": v(-16.98, 7.46) * mm});
            skLineSegment(sketch, "E38.1.1.2", {"start": v(-17.44, 7.12) * mm, "end": v(-16.98, 7.46) * mm});
            skLineSegment(sketch, "E38.1.1.3", {"start": v(-17.44, 7.12) * mm, "end": v(-17.26, 6.57) * mm});
            skLineSegment(sketch, "E38.1.1.4", {"start": v(-17.26, 6.57) * mm, "end": v(-17.73, 6.91) * mm});
            skLineSegment(sketch, "E38.1.1.5", {"start": v(-18.2, 6.57) * mm, "end": v(-17.73, 6.91) * mm});
            skLineSegment(sketch, "E38.1.1.6", {"start": v(-18.2, 6.57) * mm, "end": v(-18.02, 7.12) * mm});
            skLineSegment(sketch, "E38.1.1.7", {"start": v(-18.02, 7.12) * mm, "end": v(-18.48, 7.46) * mm});
            skLineSegment(sketch, "E38.1.1.8", {"start": v(-18.48, 7.46) * mm, "end": v(-17.9, 7.46) * mm});
            skLineSegment(sketch, "E38.1.1.9", {"start": v(-17.9, 7.46) * mm, "end": v(-17.73, 8) * mm});
            skLineSegment(sketch, "E38.1.2.0", {"start": v(-17.73, 5.26) * mm, "end": v(-17.55, 4.71) * mm});
            skLineSegment(sketch, "E38.1.2.1", {"start": v(-17.55, 4.71) * mm, "end": v(-16.98, 4.71) * mm});
            skLineSegment(sketch, "E38.1.2.2", {"start": v(-17.44, 4.38) * mm, "end": v(-16.98, 4.71) * mm});
            skLineSegment(sketch, "E38.1.2.3", {"start": v(-17.44, 4.38) * mm, "end": v(-17.26, 3.83) * mm});
            skLineSegment(sketch, "E38.1.2.4", {"start": v(-17.26, 3.83) * mm, "end": v(-17.73, 4.17) * mm});
            skLineSegment(sketch, "E38.1.2.5", {"start": v(-18.2, 3.83) * mm, "end": v(-17.73, 4.17) * mm});
            skLineSegment(sketch, "E38.1.2.6", {"start": v(-18.2, 3.83) * mm, "end": v(-18.02, 4.38) * mm});
            skLineSegment(sketch, "E38.1.2.7", {"start": v(-18.02, 4.38) * mm, "end": v(-18.48, 4.71) * mm});
            skLineSegment(sketch, "E38.1.2.8", {"start": v(-18.48, 4.71) * mm, "end": v(-17.9, 4.71) * mm});
            skLineSegment(sketch, "E38.1.2.9", {"start": v(-17.9, 4.71) * mm, "end": v(-17.73, 5.26) * mm});
            skLineSegment(sketch, "E38.1.3.0", {"start": v(-17.73, 2.52) * mm, "end": v(-17.55, 1.97) * mm});
            skLineSegment(sketch, "E38.1.3.1", {"start": v(-17.55, 1.97) * mm, "end": v(-16.98, 1.97) * mm});
            skLineSegment(sketch, "E38.1.3.2", {"start": v(-17.44, 1.63) * mm, "end": v(-16.98, 1.97) * mm});
            skLineSegment(sketch, "E38.1.3.3", {"start": v(-17.44, 1.63) * mm, "end": v(-17.26, 1.09) * mm});
            skLineSegment(sketch, "E38.1.3.4", {"start": v(-17.26, 1.09) * mm, "end": v(-17.73, 1.43) * mm});
            skLineSegment(sketch, "E38.1.3.5", {"start": v(-18.2, 1.09) * mm, "end": v(-17.73, 1.43) * mm});
            skLineSegment(sketch, "E38.1.3.6", {"start": v(-18.2, 1.09) * mm, "end": v(-18.02, 1.63) * mm});
            skLineSegment(sketch, "E38.1.3.7", {"start": v(-18.02, 1.63) * mm, "end": v(-18.48, 1.97) * mm});
            skLineSegment(sketch, "E38.1.3.8", {"start": v(-18.48, 1.97) * mm, "end": v(-17.9, 1.97) * mm});
            skLineSegment(sketch, "E38.1.3.9", {"start": v(-17.9, 1.97) * mm, "end": v(-17.73, 2.52) * mm});
            skLineSegment(sketch, "E38.2.0.0", {"start": v(-14.53, 10.75) * mm, "end": v(-14.35, 10.2) * mm});
            skLineSegment(sketch, "E38.2.0.1", {"start": v(-14.35, 10.2) * mm, "end": v(-13.78, 10.2) * mm});
            skLineSegment(sketch, "E38.2.0.2", {"start": v(-14.24, 9.86) * mm, "end": v(-13.78, 10.2) * mm});
            skLineSegment(sketch, "E38.2.0.3", {"start": v(-14.24, 9.86) * mm, "end": v(-14.06, 9.32) * mm});
            skLineSegment(sketch, "E38.2.0.4", {"start": v(-14.06, 9.32) * mm, "end": v(-14.53, 9.66) * mm});
            skLineSegment(sketch, "E38.2.0.5", {"start": v(-15, 9.32) * mm, "end": v(-14.53, 9.66) * mm});
            skLineSegment(sketch, "E38.2.0.6", {"start": v(-15, 9.32) * mm, "end": v(-14.82, 9.86) * mm});
            skLineSegment(sketch, "E38.2.0.7", {"start": v(-14.82, 9.86) * mm, "end": v(-15.28, 10.2) * mm});
            skLineSegment(sketch, "E38.2.0.8", {"start": v(-15.28, 10.2) * mm, "end": v(-14.7, 10.2) * mm});
            skLineSegment(sketch, "E38.2.0.9", {"start": v(-14.7, 10.2) * mm, "end": v(-14.53, 10.75) * mm});
            skLineSegment(sketch, "E38.2.1.0", {"start": v(-14.53, 8) * mm, "end": v(-14.35, 7.46) * mm});
            skLineSegment(sketch, "E38.2.1.1", {"start": v(-14.35, 7.46) * mm, "end": v(-13.78, 7.46) * mm});
            skLineSegment(sketch, "E38.2.1.2", {"start": v(-14.24, 7.12) * mm, "end": v(-13.78, 7.46) * mm});
            skLineSegment(sketch, "E38.2.1.3", {"start": v(-14.24, 7.12) * mm, "end": v(-14.06, 6.57) * mm});
            skLineSegment(sketch, "E38.2.1.4", {"start": v(-14.06, 6.57) * mm, "end": v(-14.53, 6.91) * mm});
            skLineSegment(sketch, "E38.2.1.5", {"start": v(-15, 6.57) * mm, "end": v(-14.53, 6.91) * mm});
            skLineSegment(sketch, "E38.2.1.6", {"start": v(-15, 6.57) * mm, "end": v(-14.82, 7.12) * mm});
            skLineSegment(sketch, "E38.2.1.7", {"start": v(-14.82, 7.12) * mm, "end": v(-15.28, 7.46) * mm});
            skLineSegment(sketch, "E38.2.1.8", {"start": v(-15.28, 7.46) * mm, "end": v(-14.7, 7.46) * mm});
            skLineSegment(sketch, "E38.2.1.9", {"start": v(-14.7, 7.46) * mm, "end": v(-14.53, 8) * mm});
            skLineSegment(sketch, "E38.2.2.0", {"start": v(-14.53, 5.26) * mm, "end": v(-14.35, 4.71) * mm});
            skLineSegment(sketch, "E38.2.2.1", {"start": v(-14.35, 4.71) * mm, "end": v(-13.78, 4.71) * mm});
            skLineSegment(sketch, "E38.2.2.2", {"start": v(-14.24, 4.38) * mm, "end": v(-13.78, 4.71) * mm});
            skLineSegment(sketch, "E38.2.2.3", {"start": v(-14.24, 4.38) * mm, "end": v(-14.06, 3.83) * mm});
            skLineSegment(sketch, "E38.2.2.4", {"start": v(-14.06, 3.83) * mm, "end": v(-14.53, 4.17) * mm});
            skLineSegment(sketch, "E38.2.2.5", {"start": v(-15, 3.83) * mm, "end": v(-14.53, 4.17) * mm});
            skLineSegment(sketch, "E38.2.2.6", {"start": v(-15, 3.83) * mm, "end": v(-14.82, 4.38) * mm});
            skLineSegment(sketch, "E38.2.2.7", {"start": v(-14.82, 4.38) * mm, "end": v(-15.28, 4.71) * mm});
            skLineSegment(sketch, "E38.2.2.8", {"start": v(-15.28, 4.71) * mm, "end": v(-14.7, 4.71) * mm});
            skLineSegment(sketch, "E38.2.2.9", {"start": v(-14.7, 4.71) * mm, "end": v(-14.53, 5.26) * mm});
            skLineSegment(sketch, "E38.2.3.0", {"start": v(-14.53, 2.52) * mm, "end": v(-14.35, 1.97) * mm});
            skLineSegment(sketch, "E38.2.3.1", {"start": v(-14.35, 1.97) * mm, "end": v(-13.78, 1.97) * mm});
            skLineSegment(sketch, "E38.2.3.2", {"start": v(-14.24, 1.63) * mm, "end": v(-13.78, 1.97) * mm});
            skLineSegment(sketch, "E38.2.3.3", {"start": v(-14.24, 1.63) * mm, "end": v(-14.06, 1.09) * mm});
            skLineSegment(sketch, "E38.2.3.4", {"start": v(-14.06, 1.09) * mm, "end": v(-14.53, 1.43) * mm});
            skLineSegment(sketch, "E38.2.3.5", {"start": v(-15, 1.09) * mm, "end": v(-14.53, 1.43) * mm});
            skLineSegment(sketch, "E38.2.3.6", {"start": v(-15, 1.09) * mm, "end": v(-14.82, 1.63) * mm});
            skLineSegment(sketch, "E38.2.3.7", {"start": v(-14.82, 1.63) * mm, "end": v(-15.28, 1.97) * mm});
            skLineSegment(sketch, "E38.2.3.8", {"start": v(-15.28, 1.97) * mm, "end": v(-14.7, 1.97) * mm});
            skLineSegment(sketch, "E38.2.3.9", {"start": v(-14.7, 1.97) * mm, "end": v(-14.53, 2.52) * mm});
            skLineSegment(sketch, "E38.3.0.0", {"start": v(-11.33, 10.75) * mm, "end": v(-11.15, 10.2) * mm});
            skLineSegment(sketch, "E38.3.0.1", {"start": v(-11.15, 10.2) * mm, "end": v(-10.58, 10.2) * mm});
            skLineSegment(sketch, "E38.3.0.2", {"start": v(-11.04, 9.86) * mm, "end": v(-10.58, 10.2) * mm});
            skLineSegment(sketch, "E38.3.0.3", {"start": v(-11.04, 9.86) * mm, "end": v(-10.86, 9.32) * mm});
            skLineSegment(sketch, "E38.3.0.4", {"start": v(-10.86, 9.32) * mm, "end": v(-11.33, 9.66) * mm});
            skLineSegment(sketch, "E38.3.0.5", {"start": v(-11.8, 9.32) * mm, "end": v(-11.33, 9.66) * mm});
            skLineSegment(sketch, "E38.3.0.6", {"start": v(-11.8, 9.32) * mm, "end": v(-11.62, 9.86) * mm});
            skLineSegment(sketch, "E38.3.0.7", {"start": v(-11.62, 9.86) * mm, "end": v(-12.08, 10.2) * mm});
            skLineSegment(sketch, "E38.3.0.8", {"start": v(-12.08, 10.2) * mm, "end": v(-11.5, 10.2) * mm});
            skLineSegment(sketch, "E38.3.0.9", {"start": v(-11.5, 10.2) * mm, "end": v(-11.33, 10.75) * mm});
            skLineSegment(sketch, "E38.3.1.0", {"start": v(-11.33, 8) * mm, "end": v(-11.15, 7.46) * mm});
            skLineSegment(sketch, "E38.3.1.1", {"start": v(-11.15, 7.46) * mm, "end": v(-10.58, 7.46) * mm});
            skLineSegment(sketch, "E38.3.1.2", {"start": v(-11.04, 7.12) * mm, "end": v(-10.58, 7.46) * mm});
            skLineSegment(sketch, "E38.3.1.3", {"start": v(-11.04, 7.12) * mm, "end": v(-10.86, 6.57) * mm});
            skLineSegment(sketch, "E38.3.1.4", {"start": v(-10.86, 6.57) * mm, "end": v(-11.33, 6.91) * mm});
            skLineSegment(sketch, "E38.3.1.5", {"start": v(-11.8, 6.57) * mm, "end": v(-11.33, 6.91) * mm});
            skLineSegment(sketch, "E38.3.1.6", {"start": v(-11.8, 6.57) * mm, "end": v(-11.62, 7.12) * mm});
            skLineSegment(sketch, "E38.3.1.7", {"start": v(-11.62, 7.12) * mm, "end": v(-12.08, 7.46) * mm});
            skLineSegment(sketch, "E38.3.1.8", {"start": v(-12.08, 7.46) * mm, "end": v(-11.5, 7.46) * mm});
            skLineSegment(sketch, "E38.3.1.9", {"start": v(-11.5, 7.46) * mm, "end": v(-11.33, 8) * mm});
            skLineSegment(sketch, "E38.3.2.0", {"start": v(-11.33, 5.26) * mm, "end": v(-11.15, 4.71) * mm});
            skLineSegment(sketch, "E38.3.2.1", {"start": v(-11.15, 4.71) * mm, "end": v(-10.58, 4.71) * mm});
            skLineSegment(sketch, "E38.3.2.2", {"start": v(-11.04, 4.38) * mm, "end": v(-10.58, 4.71) * mm});
            skLineSegment(sketch, "E38.3.2.3", {"start": v(-11.04, 4.38) * mm, "end": v(-10.86, 3.83) * mm});
            skLineSegment(sketch, "E38.3.2.4", {"start": v(-10.86, 3.83) * mm, "end": v(-11.33, 4.17) * mm});
            skLineSegment(sketch, "E38.3.2.5", {"start": v(-11.8, 3.83) * mm, "end": v(-11.33, 4.17) * mm});
            skLineSegment(sketch, "E38.3.2.6", {"start": v(-11.8, 3.83) * mm, "end": v(-11.62, 4.38) * mm});
            skLineSegment(sketch, "E38.3.2.7", {"start": v(-11.62, 4.38) * mm, "end": v(-12.08, 4.71) * mm});
            skLineSegment(sketch, "E38.3.2.8", {"start": v(-12.08, 4.71) * mm, "end": v(-11.5, 4.71) * mm});
            skLineSegment(sketch, "E38.3.2.9", {"start": v(-11.5, 4.71) * mm, "end": v(-11.33, 5.26) * mm});
            skLineSegment(sketch, "E38.3.3.0", {"start": v(-11.33, 2.52) * mm, "end": v(-11.15, 1.97) * mm});
            skLineSegment(sketch, "E38.3.3.1", {"start": v(-11.15, 1.97) * mm, "end": v(-10.58, 1.97) * mm});
            skLineSegment(sketch, "E38.3.3.2", {"start": v(-11.04, 1.63) * mm, "end": v(-10.58, 1.97) * mm});
            skLineSegment(sketch, "E38.3.3.3", {"start": v(-11.04, 1.63) * mm, "end": v(-10.86, 1.09) * mm});
            skLineSegment(sketch, "E38.3.3.4", {"start": v(-10.86, 1.09) * mm, "end": v(-11.33, 1.43) * mm});
            skLineSegment(sketch, "E38.3.3.5", {"start": v(-11.8, 1.09) * mm, "end": v(-11.33, 1.43) * mm});
            skLineSegment(sketch, "E38.3.3.6", {"start": v(-11.8, 1.09) * mm, "end": v(-11.62, 1.63) * mm});
            skLineSegment(sketch, "E38.3.3.7", {"start": v(-11.62, 1.63) * mm, "end": v(-12.08, 1.97) * mm});
            skLineSegment(sketch, "E38.3.3.8", {"start": v(-12.08, 1.97) * mm, "end": v(-11.5, 1.97) * mm});
            skLineSegment(sketch, "E38.3.3.9", {"start": v(-11.5, 1.97) * mm, "end": v(-11.33, 2.52) * mm});
            skLineSegment(sketch, "E38.4.0.0", {"start": v(-8.13, 10.75) * mm, "end": v(-7.95, 10.2) * mm});
            skLineSegment(sketch, "E38.4.0.1", {"start": v(-7.95, 10.2) * mm, "end": v(-7.38, 10.2) * mm});
            skLineSegment(sketch, "E38.4.0.2", {"start": v(-7.84, 9.86) * mm, "end": v(-7.38, 10.2) * mm});
            skLineSegment(sketch, "E38.4.0.3", {"start": v(-7.84, 9.86) * mm, "end": v(-7.66, 9.32) * mm});
            skLineSegment(sketch, "E38.4.0.4", {"start": v(-7.66, 9.32) * mm, "end": v(-8.13, 9.66) * mm});
            skLineSegment(sketch, "E38.4.0.5", {"start": v(-8.6, 9.32) * mm, "end": v(-8.13, 9.66) * mm});
            skLineSegment(sketch, "E38.4.0.6", {"start": v(-8.6, 9.32) * mm, "end": v(-8.41, 9.86) * mm});
            skLineSegment(sketch, "E38.4.0.7", {"start": v(-8.41, 9.86) * mm, "end": v(-8.88, 10.2) * mm});
            skLineSegment(sketch, "E38.4.0.8", {"start": v(-8.88, 10.2) * mm, "end": v(-8.3, 10.2) * mm});
            skLineSegment(sketch, "E38.4.0.9", {"start": v(-8.3, 10.2) * mm, "end": v(-8.13, 10.75) * mm});
            skLineSegment(sketch, "E38.4.1.0", {"start": v(-8.13, 8) * mm, "end": v(-7.95, 7.46) * mm});
            skLineSegment(sketch, "E38.4.1.1", {"start": v(-7.95, 7.46) * mm, "end": v(-7.38, 7.46) * mm});
            skLineSegment(sketch, "E38.4.1.2", {"start": v(-7.84, 7.12) * mm, "end": v(-7.38, 7.46) * mm});
            skLineSegment(sketch, "E38.4.1.3", {"start": v(-7.84, 7.12) * mm, "end": v(-7.66, 6.57) * mm});
            skLineSegment(sketch, "E38.4.1.4", {"start": v(-7.66, 6.57) * mm, "end": v(-8.13, 6.91) * mm});
            skLineSegment(sketch, "E38.4.1.5", {"start": v(-8.6, 6.57) * mm, "end": v(-8.13, 6.91) * mm});
            skLineSegment(sketch, "E38.4.1.6", {"start": v(-8.6, 6.57) * mm, "end": v(-8.41, 7.12) * mm});
            skLineSegment(sketch, "E38.4.1.7", {"start": v(-8.41, 7.12) * mm, "end": v(-8.88, 7.46) * mm});
            skLineSegment(sketch, "E38.4.1.8", {"start": v(-8.88, 7.46) * mm, "end": v(-8.3, 7.46) * mm});
            skLineSegment(sketch, "E38.4.1.9", {"start": v(-8.3, 7.46) * mm, "end": v(-8.13, 8) * mm});
            skLineSegment(sketch, "E38.4.2.0", {"start": v(-8.13, 5.26) * mm, "end": v(-7.95, 4.71) * mm});
            skLineSegment(sketch, "E38.4.2.1", {"start": v(-7.95, 4.71) * mm, "end": v(-7.38, 4.71) * mm});
            skLineSegment(sketch, "E38.4.2.2", {"start": v(-7.84, 4.38) * mm, "end": v(-7.38, 4.71) * mm});
            skLineSegment(sketch, "E38.4.2.3", {"start": v(-7.84, 4.38) * mm, "end": v(-7.66, 3.83) * mm});
            skLineSegment(sketch, "E38.4.2.4", {"start": v(-7.66, 3.83) * mm, "end": v(-8.13, 4.17) * mm});
            skLineSegment(sketch, "E38.4.2.5", {"start": v(-8.6, 3.83) * mm, "end": v(-8.13, 4.17) * mm});
            skLineSegment(sketch, "E38.4.2.6", {"start": v(-8.6, 3.83) * mm, "end": v(-8.41, 4.38) * mm});
            skLineSegment(sketch, "E38.4.2.7", {"start": v(-8.41, 4.38) * mm, "end": v(-8.88, 4.71) * mm});
            skLineSegment(sketch, "E38.4.2.8", {"start": v(-8.88, 4.71) * mm, "end": v(-8.3, 4.71) * mm});
            skLineSegment(sketch, "E38.4.2.9", {"start": v(-8.3, 4.71) * mm, "end": v(-8.13, 5.26) * mm});
            skLineSegment(sketch, "E38.4.3.0", {"start": v(-8.13, 2.52) * mm, "end": v(-7.95, 1.97) * mm});
            skLineSegment(sketch, "E38.4.3.1", {"start": v(-7.95, 1.97) * mm, "end": v(-7.38, 1.97) * mm});
            skLineSegment(sketch, "E38.4.3.2", {"start": v(-7.84, 1.63) * mm, "end": v(-7.38, 1.97) * mm});
            skLineSegment(sketch, "E38.4.3.3", {"start": v(-7.84, 1.63) * mm, "end": v(-7.66, 1.09) * mm});
            skLineSegment(sketch, "E38.4.3.4", {"start": v(-7.66, 1.09) * mm, "end": v(-8.13, 1.43) * mm});
            skLineSegment(sketch, "E38.4.3.5", {"start": v(-8.6, 1.09) * mm, "end": v(-8.13, 1.43) * mm});
            skLineSegment(sketch, "E38.4.3.6", {"start": v(-8.6, 1.09) * mm, "end": v(-8.41, 1.63) * mm});
            skLineSegment(sketch, "E38.4.3.7", {"start": v(-8.41, 1.63) * mm, "end": v(-8.88, 1.97) * mm});
            skLineSegment(sketch, "E38.4.3.8", {"start": v(-8.88, 1.97) * mm, "end": v(-8.3, 1.97) * mm});
            skLineSegment(sketch, "E38.4.3.9", {"start": v(-8.3, 1.97) * mm, "end": v(-8.13, 2.52) * mm});
            skLineSegment(sketch, "E38.direction1", {"start": v(-20.75, 10.2) * mm, "end": v(-17.55, 10.2) * mm, "construction": true});
            skLineSegment(sketch, "E38.direction2", {"start": v(-20.75, 10.2) * mm, "end": v(-20.75, 7.46) * mm, "construction": true});
            skSolve(sketch);
        }
        {
            var Q0;
            {var subQ0=sQuery(id+"F0.wireOp",EDGE,"E12.MirrorCS");Q0=makeQuery(id+"F0.imprint","IMPRINT",FACE,{"disambiguationData":[TD([[makeQuery(id+"F0.imprint","IMPRINT",EDGE,{"derivedFrom":subQ0}),-1.0]])]});}
            var Q1;
            {var subQ0=sQuery(id+"F0.wireOp",EDGE,"E10.MirrorCS");Q1=makeQuery(id+"F0.imprint","IMPRINT",FACE,{"disambiguationData":[TD([[makeQuery(id+"F0.imprint","IMPRINT",EDGE,{"derivedFrom":subQ0}),-1.0]])]});}
            var Q2;
            Q2=makeQuery(id+"F0.imprint","IMPRINT",FACE,{"disambiguationData":[TD([[makeQuery(id+"F0.imprint","IMPRINT",EDGE,{"derivedFrom":sQuery(id+"F0.wireOp",EDGE,"E9.top")}),1.0]])]});
            var Q3;
            {var subQ0=sQuery(id+"F0.wireOp",EDGE,"E6.MirrorCS");Q3=makeQuery(id+"F0.imprint","IMPRINT",FACE,{"disambiguationData":[TD([[makeQuery(id+"F0.imprint","IMPRINT",EDGE,{"derivedFrom":subQ0}),-1.0]])]});}
            var Q4;
            {var subQ0=sQuery(id+"F0.wireOp",EDGE,"E4.MirrorCS");Q4=makeQuery(id+"F0.imprint","IMPRINT",FACE,{"disambiguationData":[TD([[makeQuery(id+"F0.imprint","IMPRINT",EDGE,{"derivedFrom":subQ0}),-1.0]])]});}
            var Q5;
            {var subQ0=sQuery(id+"F0.wireOp",EDGE,"E2.top");Q5=makeQuery(id+"F0.imprint","IMPRINT",FACE,{"disambiguationData":[TD([[makeQuery(id+"F0.imprint","IMPRINT",EDGE,{"derivedFrom":subQ0}),-1.0]])]});}
            extrude(context, id + "F1", {"entities" : qUnion([Q0, Q1, Q2, Q3, Q4, Q5]), "depth" : 2 * mm, "offsetDistance" : 25.4 * mm});
        }
        {
            var Q0;
            Q0=qCreatedBy(makeId("Top.planeOp"),FACE);
            var sketch = newSketch(context, id + "F2", { "sketchPlane" : qUnion([Q0])});
            skLineSegment(sketch, "E39.bottom", {"start": v(28.58, 15.88) * mm, "end": v(-28.57, 15.88) * mm});
            skLineSegment(sketch, "E39.top", {"start": v(28.57, -15.88) * mm, "end": v(-28.58, -15.88) * mm});
            skLineSegment(sketch, "E39.left", {"start": v(28.58, 15.88) * mm, "end": v(28.57, -15.87) * mm});
            skLineSegment(sketch, "E39.right", {"start": v(-28.57, 15.88) * mm, "end": v(-28.58, -15.88) * mm});
            skPoint(sketch, "E39.middle", {"position": v(0, 0) * mm});
            skLineSegment(sketch, "E40.0", {"start": v(28.83, 16.13) * mm, "end": v(-28.83, 16.13) * mm});
            skLineSegment(sketch, "E40.1", {"start": v(28.83, 16.13) * mm, "end": v(28.83, -16.13) * mm});
            skLineSegment(sketch, "E40.2", {"start": v(28.83, -16.13) * mm, "end": v(-28.83, -16.13) * mm});
            skLineSegment(sketch, "E40.3", {"start": v(-28.83, 16.13) * mm, "end": v(-28.83, -16.13) * mm});
            skSolve(sketch);
        }
        {
            var Q0;
            Q0=qSketchRegion(id+"F2",true);
            extrude(context, id + "F3", {"entities" : qUnion([Q0]), "depth" : 2 * mm, "offsetDistance" : 25.4 * mm});
        }
        {
            var Q0;
            Q0=qCreatedBy(makeId("Top.planeOp"),FACE);
            var sketch = newSketch(context, id + "F4", { "sketchPlane" : qUnion([Q0])});
            skLineSegment(sketch, "E41.bottom", {"start": v(28.58, 15.88) * mm, "end": v(-28.57, 15.88) * mm});
            skLineSegment(sketch, "E41.top", {"start": v(28.57, -15.88) * mm, "end": v(-28.58, -15.88) * mm});
            skLineSegment(sketch, "E41.left", {"start": v(28.58, 15.88) * mm, "end": v(28.57, -15.88) * mm});
            skLineSegment(sketch, "E41.right", {"start": v(-28.57, 15.88) * mm, "end": v(-28.58, -15.88) * mm});
            skPoint(sketch, "E41.middle", {"position": v(0, 0) * mm});
            skSolve(sketch);
        }
        {
            var Q0;
            Q0=qSketchRegion(id+"F4",true);
            extrude(context, id + "F5", {"entities" : qUnion([Q0]), "depth" : .5 * mm, "offsetDistance" : 25.4 * mm});
        }
    });
